# Revit family: xxShower_Spray-American_Standard-Extender-1660.130
name_source: partatom
category: Plumbing Fixtures
revit_build: Autodesk Revit 2014 (Build: 20130308_1515(x64)
units: mm (PartAtom-declared; Revit-internal decimal feet)

## types (1)
- 1660.130
    Assembly Code = D2010710
    CW Connection = Yes
    CWFU = 3
    Default Elevation = 54"
    Description = Extender Multifunction Body Spray
    Finish = Brass-American Standard-002-Polished Chrome
    Flow Rate = 1.5 gpm/ 5.7 L/min
    HW Connection = Yes
    HWFU = 3
    Height = 2 15/16"
    Inlet From Finished Wall = 2 1/2"
    Installation Type = Wall Mounted
    Length = 2 15/16"
    Manufacturer = American Standard
    Material = Brass-American Standard-002-Polished Chrome
    Model = 1660.130
    Price = Prices may vary. Please consult Manufacturer Representative for most up-to-date price list.
    Product Documentation Link = https://www.americanstandard-us.com
    Product Page URL = https://www.americanstandard-us.com
    Specification = Body Spray shall be flush mount to wall projecting no more than 1/2" when not in use. Body spray shall have at least 3 spray patterns. Features an automatic swivel spray that extends when water is turned on and retracts when water is turned off. Fitting shall be American Standard Model 1660.130.
    Tempered Water Connection Diameter = 1/2"
    Tempered Water Connection Radius = 1/4"
    URL = https://www.americanstandard-us.com
    Vent Connection = No
    WFU = 4
    Warranty Information = https://www.americanstandard-us.com
    Waste Connection = No
    Width = 1/2"

## geometry (parser evidence)
native form markers: Sweep x1
no freeform markers — native parametric forms only
